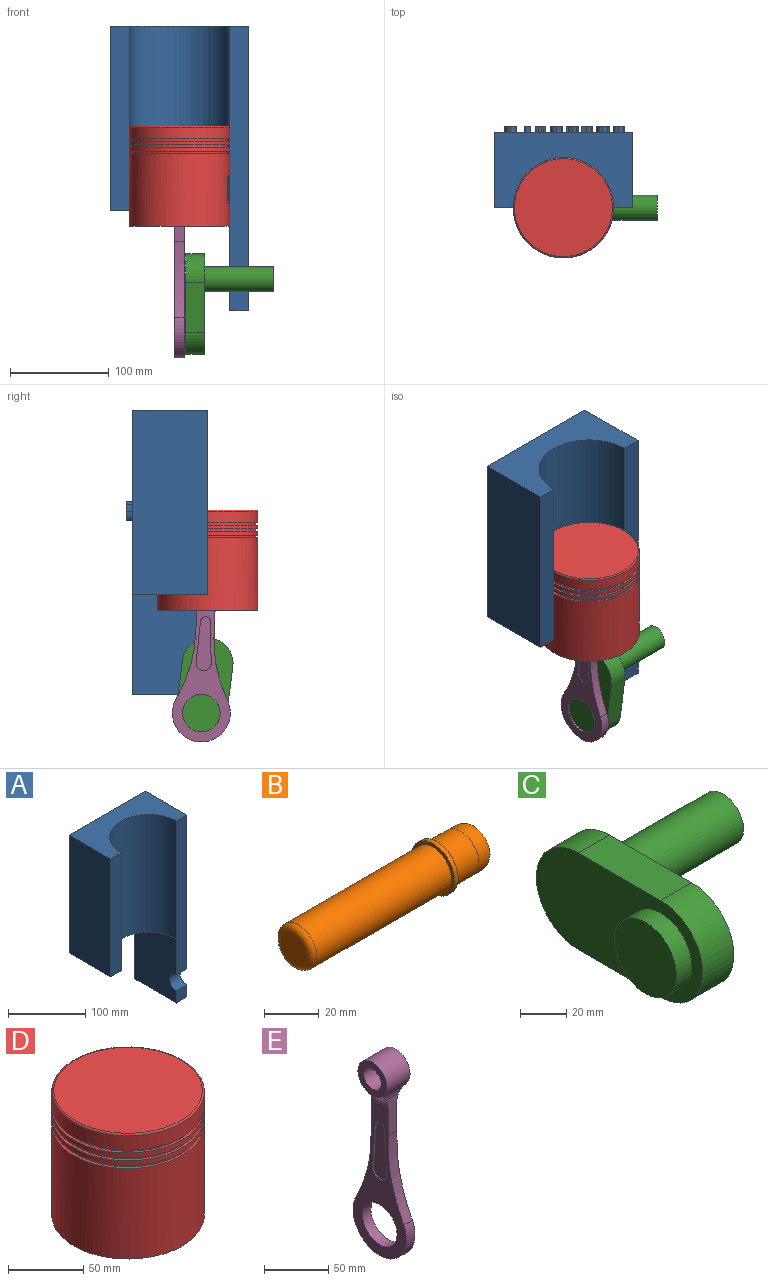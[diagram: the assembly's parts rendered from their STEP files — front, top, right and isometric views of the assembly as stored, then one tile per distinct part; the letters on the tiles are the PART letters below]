
ASSEMBLY  parts=5 mates=6
PART A: 146 faces, bbox 139.7x82.6x288.3 mm
  f0: plane 288.32x139.7mm, normal (0,1,0), area 27175.9mm2, adj f2,f3,f6,f8,f9,f10,f18,f19
  f1: plane 243.87x19.05mm, normal (0,-1,0), area 4645.6mm2, adj f2,f4,f8,f9,f11
  f2: plane 288.32x76.2mm, normal (1,0,0), area 21716.3mm2, adj f0,f1,f5,f8,f10,f11
  f3: plane 120.65x76.2mm, normal (0,0,-1), area 5139.9mm2, adj f0,f4,f6,f7,f9
  f4: cylinder r=50.8mm len=186.72mm, axis (0,0,-1), area 29798.5mm2, adj f1,f3,f7,f8
  f5: plane 19.05x19.05mm, normal (0,-1,0), area 362.9mm2, adj f2,f9,f10,f11
  f6: plane 186.72x76.2mm, normal (-1,0,0), area 14227.7mm2, adj f0,f3,f7,f8
  f7: plane 186.72x19.05mm, normal (0,-1,0), area 3556.9mm2, adj f3,f4,f6,f8
  f8: plane 139.7x76.2mm, normal (0,0,1), area 6591.5mm2, adj f0,f1,f2,f4,f6,f7
  f9: plane 101.6x76.2mm, normal (-1,0,0), area 7488.6mm2, adj f0,f1,f3,f5,f10,f11
  f10: plane 76.2x19.05mm, normal (0,0,-1), area 1451.6mm2, adj f0,f2,f5,f9
  f11: cylinder r=12.7mm len=25.4mm, axis (1,0,0), area 760.1mm2, adj f1,f2,f5,f9
  f12: plane 6.35x2.06mm, normal (-0.04,0,-1), area 13.1mm2, adj f13,f35,f36,f37
  f13: plane 6.35x1.26mm, normal (1,0,0), area 8mm2, adj f12,f14,f36,f37
  f14: extruded ~6.35x2.92mm, area 20.4mm2, adj f13,f15,f36,f37
  f15: extruded ~6.35x2.98mm, area 20.5mm2, adj f14,f16,f36,f37
  f16: extruded ~6.35x2.54mm, area 24.8mm2, adj f15,f17,f36,f37
  f17: extruded ~6.35x2.08mm, area 15.4mm2, adj f16,f35,f36,f37
  f18: plane 6.35x1.93mm, normal (0.97,0,-0.24), area 12.6mm2, adj f0,f19,f34,f36
  f19: plane 6.35x1.66mm, normal (0,0,-1), area 10.6mm2, adj f0,f18,f20,f36
  f20: plane 9.56x6.35mm, normal (-1,0,0), area 60.7mm2, adj f0,f19,f21,f36
  f21: extruded ~6.35x3.55mm, area 24.7mm2, adj f0,f20,f22,f36
  f22: extruded ~6.35x4.17mm, area 28mm2, adj f0,f21,f23,f36
  f23: extruded ~6.35x4.87mm, area 32.2mm2, adj f0,f22,f24,f36
  f24: plane 6.35x1.74mm, normal (0.91,0,-0.42), area 12.2mm2, adj f0,f23,f25,f36
  f25: extruded ~6.35x4.17mm, area 27.5mm2, adj f0,f24,f26,f36
  f26: extruded ~6.35x3.1mm, area 31.4mm2, adj f0,f25,f27,f36
  f27: plane 6.35x0.87mm, normal (1,0,0), area 5.6mm2, adj f0,f26,f28,f36
  f28: plane 6.35x2.58mm, normal (0.03,0,1), area 16.4mm2, adj f0,f27,f29,f36
  f29: extruded ~6.48x6.35mm, area 56.1mm2, adj f0,f28,f30,f36
  f30: extruded ~6.35x3.06mm, area 21.5mm2, adj f0,f29,f31,f36
  f31: extruded ~6.35x3.25mm, area 22.3mm2, adj f0,f30,f32,f36
  f32: extruded ~6.35x2.66mm, area 17.3mm2, adj f0,f31,f33,f36
  f33: extruded ~6.35x2.01mm, area 16.9mm2, adj f0,f32,f34,f36
  f34: plane 6.35x0.1mm, normal (0,0,-1), area 0.6mm2, adj f0,f18,f33,f36
  f35: extruded ~6.35x3.53mm, area 23.2mm2, adj f12,f17,f36,f37
  f36: plane 14.47x11.32mm, normal (0,1,0), area 83mm2, adj f12,f13,f14,f15,f16,f17,f18,f19
  f37: plane 6.63x5.21mm, normal (0,1,0), area 27.9mm2, adj f12,f13,f14,f15,f16,f17,f35
  f38: plane 7.28x6.35mm, normal (0,0,1), area 46.2mm2, adj f39,f52,f53,f54
  f39: extruded ~6.35x3.88mm, area 38.9mm2, adj f38,f52,f53,f54
  f40: plane 9.84x6.35mm, normal (0,0,-1), area 62.5mm2, adj f0,f41,f51,f53
  f41: plane 6.35x1.44mm, normal (-1,0,0), area 9.1mm2, adj f0,f40,f42,f53
  f42: extruded ~6.35x4.54mm, area 31.4mm2, adj f0,f41,f43,f53
  f43: extruded ~6.35x4.3mm, area 30.3mm2, adj f0,f42,f44,f53
  f44: extruded ~6.35x4.61mm, area 32.9mm2, adj f0,f43,f45,f53
  f45: extruded ~6.35x5.36mm, area 36.5mm2, adj f0,f44,f46,f53
  f46: extruded ~6.35x5.23mm, area 36.2mm2, adj f0,f45,f47,f53
  f47: extruded ~6.35x4.98mm, area 34.8mm2, adj f0,f46,f48,f53
  f48: extruded ~6.35x4.63mm, area 30.2mm2, adj f0,f47,f49,f53
  f49: plane 6.35x2.03mm, normal (-1,0,0), area 12.9mm2, adj f0,f48,f50,f53
  f50: extruded ~6.35x4.71mm, area 30.7mm2, adj f0,f49,f51,f53
  f51: extruded ~6.35x4.77mm, area 46.9mm2, adj f0,f40,f50,f53
  f52: extruded ~6.35x3.88mm, area 37.8mm2, adj f38,f39,f53,f54
  f53: plane 14.47x12.24mm, normal (0,1,0), area 84.4mm2, adj f38,f39,f40,f41,f42,f43,f44,f45
  f54: plane 7.28x3.88mm, normal (0,1,0), area 23.1mm2, adj f38,f39,f52
  f55: plane 6.35x3.41mm, normal (0.08,0,-1), area 21.7mm2, adj f0,f56,f64,f65
  f56: plane 16.14x6.35mm, normal (1,0,0), area 102.5mm2, adj f0,f55,f57,f65
  f57: plane 6.35x4.37mm, normal (0.06,0,1), area 27.8mm2, adj f0,f56,f58,f65
  f58: plane 6.35x1.56mm, normal (1,0,0), area 9.9mm2, adj f0,f57,f59,f65
  f59: plane 11.17x6.35mm, normal (0,0,-1), area 70.9mm2, adj f0,f58,f60,f65
  f60: plane 6.35x1.56mm, normal (-1,0,0), area 9.9mm2, adj f0,f59,f61,f65
  f61: plane 6.35x4.47mm, normal (-0.06,0,1), area 28.5mm2, adj f0,f60,f62,f65
  f62: plane 17.96x6.35mm, normal (-1,0,0), area 114.1mm2, adj f0,f61,f63,f65
  f63: plane 6.35x5.73mm, normal (0,0,1), area 36.4mm2, adj f0,f62,f64,f65
  f64: plane 6.35x1.55mm, normal (1,0,0), area 9.9mm2, adj f0,f55,f63,f65
  f65: plane 19.78x11.17mm, normal (0,1,0), area 66.6mm2, adj f55,f56,f57,f58,f59,f60,f61,f62
  f66: plane 6.35x0.52mm, normal (1,0,0), area 3.3mm2, adj f67,f86,f87,f88
  f67: extruded ~6.35x3.64mm, area 24.2mm2, adj f66,f68,f87,f88
  f68: extruded ~6.35x2.78mm, area 19.8mm2, adj f67,f69,f87,f88
  f69: extruded ~6.35x5.26mm, area 45.4mm2, adj f68,f70,f87,f88
  f70: extruded ~6.35x5.36mm, area 45.9mm2, adj f69,f71,f87,f88
  f71: extruded ~6.35x2.81mm, area 20.3mm2, adj f70,f86,f87,f88
  f72: plane 6.35x0.1mm, normal (0,0,-1), area 0.6mm2, adj f0,f73,f85,f87
  f73: plane 6.35x1.87mm, normal (0.98,0,-0.18), area 12.1mm2, adj f0,f72,f74,f87
  f74: plane 6.35x1.87mm, normal (0,0,-1), area 11.9mm2, adj f0,f73,f75,f87
  f75: plane 19.78x6.35mm, normal (-1,0,0), area 125.6mm2, adj f0,f74,f76,f87
  f76: plane 6.35x2.31mm, normal (0,0,1), area 14.7mm2, adj f0,f75,f77,f87
  f77: plane 6.35x5.54mm, normal (1,0,0), area 35.2mm2, adj f0,f76,f78,f87
  f78: extruded ~6.35x2.06mm, area 13.1mm2, adj f0,f77,f79,f87
  f79: plane 6.35x0.15mm, normal (0,0,1), area 1mm2, adj f0,f78,f80,f87
  f80: extruded ~6.35x4.09mm, area 30.2mm2, adj f0,f79,f81,f87
  f81: extruded ~6.35x4mm, area 29.3mm2, adj f0,f80,f82,f87
  f82: extruded ~6.35x5.35mm, area 35.8mm2, adj f0,f81,f83,f87
  f83: extruded ~6.35x5.31mm, area 35.6mm2, adj f0,f82,f84,f87
  f84: extruded ~6.35x4.01mm, area 29.3mm2, adj f0,f83,f85,f87
  f85: extruded ~6.35x4.09mm, area 30.6mm2, adj f0,f72,f84,f87
  f86: extruded ~6.35x4.11mm, area 27.1mm2, adj f66,f71,f87,f88
  f87: plane 20.04x11.87mm, normal (0,1,0), area 100mm2, adj f66,f67,f68,f69,f70,f71,f72,f73
  f88: plane 10.63x7.15mm, normal (0,1,0), area 64.1mm2, adj f66,f67,f68,f69,f70,f71,f86
  f89: plane 7.28x6.35mm, normal (0,0,1), area 46.2mm2, adj f90,f103,f104,f105
  f90: extruded ~6.35x3.88mm, area 38.9mm2, adj f89,f103,f104,f105
  f91: plane 9.84x6.35mm, normal (0,0,-1), area 62.5mm2, adj f0,f92,f102,f104
  f92: plane 6.35x1.44mm, normal (-1,0,0), area 9.1mm2, adj f0,f91,f93,f104
  f93: extruded ~6.35x4.54mm, area 31.4mm2, adj f0,f92,f94,f104
  f94: extruded ~6.35x4.3mm, area 30.3mm2, adj f0,f93,f95,f104
  f95: extruded ~6.35x4.61mm, area 32.9mm2, adj f0,f94,f96,f104
  f96: extruded ~6.35x5.36mm, area 36.5mm2, adj f0,f95,f97,f104
  f97: extruded ~6.35x5.23mm, area 36.2mm2, adj f0,f96,f98,f104
  f98: extruded ~6.35x4.98mm, area 34.8mm2, adj f0,f97,f99,f104
  f99: extruded ~6.35x4.63mm, area 30.2mm2, adj f0,f98,f100,f104
  f100: plane 6.35x2.03mm, normal (-1,0,0), area 12.9mm2, adj f0,f99,f101,f104
  f101: extruded ~6.35x4.71mm, area 30.7mm2, adj f0,f100,f102,f104
  f102: extruded ~6.35x4.77mm, area 46.9mm2, adj f0,f91,f101,f104
  f103: extruded ~6.35x3.88mm, area 37.8mm2, adj f89,f90,f104,f105
  f104: plane 14.47x12.24mm, normal (0,1,0), area 84.4mm2, adj f89,f90,f91,f92,f93,f94,f95,f96
  f105: plane 7.28x3.88mm, normal (0,1,0), area 23.1mm2, adj f89,f90,f103
  f106: plane 6.35x2.11mm, normal (-0.96,0,-0.28), area 14mm2, adj f0,f107,f118,f119
  f107: extruded ~6.35x3.05mm, area 19.8mm2, adj f0,f106,f108,f119
  f108: extruded ~6.35x2.72mm, area 17.9mm2, adj f0,f107,f109,f119
  f109: extruded ~6.35x2.16mm, area 19.2mm2, adj f0,f108,f110,f119
  f110: plane 6.35x0.1mm, normal (0,0,1), area 0.6mm2, adj f0,f109,f111,f119
  f111: plane 6.35x2.55mm, normal (-0.99,0,0.11), area 16.3mm2, adj f0,f110,f112,f119
  f112: plane 6.35x1.88mm, normal (0,0,1), area 12mm2, adj f0,f111,f113,f119
  f113: plane 13.95x6.35mm, normal (1,0,0), area 88.6mm2, adj f0,f112,f114,f119
  f114: plane 6.35x2.31mm, normal (0,0,-1), area 14.7mm2, adj f0,f113,f115,f119
  f115: plane 7.52x6.35mm, normal (-1,0,0), area 47.8mm2, adj f0,f114,f116,f119
  f116: extruded ~6.35x3.4mm, area 23.3mm2, adj f0,f115,f117,f119
  f117: extruded ~6.35x3.2mm, area 22.2mm2, adj f0,f116,f118,f119
  f118: extruded ~6.35x2.85mm, area 18.5mm2, adj f0,f106,f117,f119
  f119: plane 14.21x10.1mm, normal (0,1,0), area 47.5mm2, adj f106,f107,f108,f109,f110,f111,f112,f113
  f120: plane 6.35x2.24mm, normal (0,0,-1), area 14.2mm2, adj f0,f121,f128,f129
  f121: plane 18.58x6.35mm, normal (-1,0,0), area 118mm2, adj f0,f120,f122,f129
  f122: plane 6.35x1.91mm, normal (0,0,1), area 12.1mm2, adj f0,f121,f123,f129
  f123: plane 6.35x4.87mm, normal (0.62,0,0.79), area 39.2mm2, adj f0,f122,f124,f129
  f124: plane 6.35x1.56mm, normal (0.79,0,-0.62), area 12.6mm2, adj f0,f123,f125,f129
  f125: plane 6.35x1.87mm, normal (-0.63,0,-0.77), area 15.4mm2, adj f0,f124,f126,f129
  f126: extruded ~6.35x1.54mm, area 13.4mm2, adj f0,f125,f127,f129
  f127: extruded ~6.35x4.59mm, area 29.1mm2, adj f0,f126,f128,f129
  f128: plane 11.6x6.35mm, normal (1,0,0), area 73.7mm2, adj f0,f120,f127,f129
  f129: plane 18.58x6.78mm, normal (0,1,0), area 51mm2, adj f120,f121,f122,f123,f124,f125,f126,f127
  f130: extruded ~6.35x2.74mm, area 22.1mm2, adj f131,f143,f144,f145
  f131: extruded ~6.35x2.7mm, area 21.8mm2, adj f130,f132,f144,f145
  f132: extruded ~6.35x5.82mm, area 37.6mm2, adj f131,f133,f144,f145
  f133: extruded ~6.35x5.8mm, area 37.5mm2, adj f132,f134,f144,f145
  f134: extruded ~6.35x2.7mm, area 21.8mm2, adj f133,f135,f144,f145
  f135: extruded ~6.35x2.74mm, area 22.1mm2, adj f134,f136,f144,f145
  f136: extruded ~6.35x5.79mm, area 37.4mm2, adj f135,f143,f144,f145
  f137: extruded ~6.35x4.41mm, area 33.7mm2, adj f0,f138,f142,f144
  f138: extruded ~9.57x6.35mm, area 80.9mm2, adj f0,f137,f139,f144
  f139: extruded ~7.1x6.35mm, area 46.6mm2, adj f0,f138,f140,f144
  f140: extruded ~6.35x4.45mm, area 33.9mm2, adj f0,f139,f141,f144
  f141: extruded ~9.56x6.35mm, area 80.6mm2, adj f0,f140,f142,f144
  f142: extruded ~7.11x6.35mm, area 46.7mm2, adj f0,f137,f141,f144
  f143: extruded ~6.35x5.82mm, area 37.6mm2, adj f130,f136,f144,f145
  f144: plane 19.13x11.87mm, normal (0,1,0), area 96.6mm2, adj f130,f131,f132,f133,f134,f135,f136,f137
  f145: plane 15.18x7.18mm, normal (0,1,0), area 92.1mm2, adj f130,f131,f132,f133,f134,f135,f136,f143
PART B: 9 faces, bbox 94x22.2x22.2 mm
  f0: cylinder r=9.53mm len=19.05mm, axis (-1,0,0), area 737.3mm2, adj f3,f8
  f1: plane 3.81x3.81mm, normal (1,0,0), area 11.4mm2, adj f8
  f2: cylinder r=11.11mm len=22.23mm, axis (-1,0,0), area 133mm2, adj f3,f4
  f3: plane 22.23x22.23mm, normal (1,0,0), area 102.9mm2, adj f0,f2
  f4: plane 22.23x22.23mm, normal (-1,0,0), area 102.9mm2, adj f2,f6
  f5: plane 13.97x13.97mm, normal (-1,0,0), area 153.3mm2, adj f7
  f6: cylinder r=9.53mm len=69.6mm, axis (-1,0,0), area 4165.1mm2, adj f4,f7
  f7: torus R=6.99mm, axis (1,0,0), area 215.6mm2, adj f5,f6
  f8: bspline ~19.05x19.05mm, area 631.1mm2, adj f0,f1
PART C: 10 faces, bbox 98.3x102.2x51.4 mm
  f0: cylinder r=19.05mm len=38.1mm, axis (1,0,0), area 1131mm2, adj f1,f7
  f1: plane 38.1x38.1mm, normal (-1,0,0), area 1140.1mm2, adj f0
  f2: cylinder r=25.72mm len=51.44mm, axis (-1,0,0), area 1539.1mm2, adj f3,f5,f6,f7
  f3: plane 50.8x19.05mm, normal (0,0,-1), area 967.7mm2, adj f2,f4,f6,f7
  f4: cylinder r=25.72mm len=51.44mm, axis (-1,0,0), area 1539.1mm2, adj f3,f5,f6,f7
  f5: plane 50.8x19.05mm, normal (0,0,1), area 967.7mm2, adj f2,f4,f6,f7
  f6: plane 102.24x51.44mm, normal (1,0,0), area 4184.1mm2, adj f2,f3,f4,f5,f8
  f7: plane 102.24x51.44mm, normal (-1,0,0), area 3550.7mm2, adj f0,f2,f3,f4,f5
  f8: cylinder r=12.7mm len=69.85mm, axis (-1,0,0), area 5573.8mm2, adj f6,f9
  f9: plane 25.4x25.4mm, normal (1,0,0), area 506.7mm2, adj f8
PART D: 39 faces, bbox 110.4x110.4x102.1 mm
  f0: cylinder r=9.53mm len=19.05mm, axis (1,0,0), area 1003.3mm2, adj f25,f32
  f1: cylinder r=50.8mm len=101.6mm, axis (0,0,1), area 22639.7mm2, adj f14,f24,f33,f34,f36,f37
  f2: cylinder r=9.53mm len=19.05mm, axis (1,0,0), area 896.9mm2, adj f23,f26
  f3: cylinder r=50.8mm len=101.6mm, axis (0,0,1), area 1216.1mm2, adj f5,f13
  f4: plane 101.6x101.6mm, normal (0,0,-1), area 660mm2, adj f6,f12
  f5: plane 101.6x101.6mm, normal (0,0,1), area 660.2mm2, adj f3,f6
  f6: cylinder r=48.68mm len=97.36mm, axis (0,0,-1), area 776.9mm2, adj f4,f5
  f7: plane 99.06x99.06mm, normal (0,0,1), area 7707mm2, adj f38
  f8: cylinder r=50.8mm len=101.6mm, axis (0,0,1), area 3648.3mm2, adj f9,f38
  f9: plane 101.6x101.6mm, normal (0,0,-1), area 659.2mm2, adj f8,f10
  f10: cylinder r=48.68mm len=97.36mm, axis (0,0,-1), area 776.9mm2, adj f9,f11
  f11: plane 101.6x101.6mm, normal (0,0,1), area 660.2mm2, adj f10,f12
  f12: cylinder r=50.8mm len=101.6mm, axis (0,0,1), area 1216.1mm2, adj f4,f11
  f13: plane 101.6x101.6mm, normal (0,0,-1), area 660mm2, adj f3,f15
  f14: plane 101.6x101.6mm, normal (0,0,1), area 659.2mm2, adj f1,f15
  f15: cylinder r=48.68mm len=97.36mm, axis (0,0,-1), area 776.9mm2, adj f13,f14
  f16: plane 19.05x19.05mm, normal (1,0,0), area 285mm2, adj f17
  f17: cylinder r=9.53mm len=31.75mm, axis (1,0,0), area 1900.2mm2, adj f16,f18
  f18: plane 25.4x25.4mm, normal (1,0,0), area 221.7mm2, adj f17,f20
  f19: plane 88.9x88.9mm, normal (0,0,-1), area 6207.2mm2, adj f22
  f20: cylinder r=12.7mm len=26.67mm, axis (-1,0,0), area 1535mm2, adj f18,f31
  f21: cylinder r=12.7mm len=26.67mm, axis (1,0,0), area 1535mm2, adj f23,f30
  f22: cylinder r=44.45mm len=91.44mm, axis (0,0,1), area 17592.5mm2, adj f19,f24,f30,f31
  f23: plane 25.4x25.4mm, normal (-1,0,0), area 221.7mm2, adj f2,f21
  f24: plane 101.6x101.6mm, normal (0,0,-1), area 1900.2mm2, adj f1,f22
  f25: plane 22.23x22.23mm, normal (-1,0,0), area 102.9mm2, adj f0,f27
  f26: plane 22.23x22.23mm, normal (1,0,0), area 102.9mm2, adj f2,f27
  f27: cylinder r=11.11mm len=22.23mm, axis (-1,0,0), area 177.3mm2, adj f25,f26
  f28: plane 31.79x25.48mm, normal (1,0,0), area 391.5mm2, adj f29,f32,f33,f34,f35,f36
  f29: plane 22.29x1.27mm, normal (0,0,1), area 18.9mm2, adj f28,f33
  f30: bspline ~71.45x63.25mm, area 3529.9mm2, adj f21,f22
  f31: bspline ~71.49x63.32mm, area 3529.4mm2, adj f20,f22
  f32: torus R=10.79mm, axis (1,0,0), area 125.2mm2, adj f0,f28
  f33: torus R=49.53mm, axis (0,0,1), area 56.3mm2, adj f1,f28,f29,f34,f36
  f34: cylinder r=1.27mm len=25.4mm, axis (0,0,1), area 10.3mm2, adj f1,f28,f33,f37
  f35: cylinder r=1.27mm len=31.32mm, axis (0,-1,0), area 31.2mm2, adj f28,f37
  f36: cylinder r=1.27mm len=25.4mm, axis (0,0,1), area 10.3mm2, adj f1,f28,f33,f37
  f37: bspline ~32.12x2.69mm, area 50.1mm2, adj f1,f34,f35,f36
  f38: torus R=49.53mm, axis (0,0,1), area 631mm2, adj f7,f8
PART E: 26 faces, bbox 35.2x61.2x187.8 mm
  f0: cylinder r=9.53mm len=25.4mm, axis (-1,0,0), area 1520.1mm2, adj f2,f3
  f1: cylinder r=15.88mm len=31.75mm, axis (-1,0,0), area 1829.5mm2, adj f2,f3,f8,f11
  f2: plane 31.75x31.75mm, normal (1,0,0), area 506.7mm2, adj f0,f1,f10
  f3: plane 31.75x31.75mm, normal (-1,0,0), area 506.7mm2, adj f0,f1,f9
  f4: plane 35.2x14.16mm, normal (0,-1,0), area 340mm2, adj f6,f7,f8,f9,f10,f14
  f5: plane 35.2x14.16mm, normal (0,1,0), area 340mm2, adj f6,f7,f9,f10,f11,f15
  f6: plane 145.49x58.64mm, normal (1,0,0), area 2910.8mm2, adj f4,f5,f10,f12,f13,f14,f15,f21
  f7: plane 145.49x58.64mm, normal (-1,0,0), area 2910.8mm2, adj f4,f5,f9,f12,f13,f14,f15,f16
  f8: cylinder r=12.7mm len=25.4mm, axis (-1,0,0), area 173.8mm2, adj f1,f4,f9,f10
  f9: torus R=27.67mm, axis (-1,0,0), area 323.1mm2, adj f3,f4,f5,f7,f8,f11
  f10: torus R=27.67mm, axis (-1,0,0), area 323.1mm2, adj f2,f4,f5,f6,f8,f11
  f11: cylinder r=12.7mm len=25.4mm, axis (-1,0,0), area 173.8mm2, adj f1,f5,f9,f10
  f12: cylinder r=29.31mm len=58.63mm, axis (-1,0,0), area 1115mm2, adj f6,f7,f14,f15
  f13: cylinder r=19.05mm len=38.1mm, axis (-1,0,0), area 1129.5mm2, adj f6,f7
  f14: bspline ~76.44x17.27mm, area 748.3mm2, adj f4,f6,f7,f12
  f15: bspline ~76.44x17.27mm, area 748.3mm2, adj f5,f6,f7,f12
  f16: plane 41.88x2.53mm, normal (0,1,-0.06), area 53.3mm2, adj f7,f17,f19,f20
  f17: cylinder r=5.09mm len=10.16mm, axis (-1,0,0), area 19.5mm2, adj f7,f16,f18,f20
  f18: plane 41.88x2.53mm, normal (0,-1,-0.06), area 53.3mm2, adj f7,f17,f19,f20
  f19: cylinder r=7.62mm len=15.25mm, axis (-1,0,0), area 31.6mm2, adj f7,f16,f18,f20
  f20: plane 54.75x15.25mm, normal (-1,0,0), area 667.4mm2, adj f16,f17,f18,f19
  f21: plane 41.88x2.53mm, normal (0,1,-0.06), area 53.3mm2, adj f6,f22,f24,f25
  f22: cylinder r=7.62mm len=15.25mm, axis (1,0,0), area 31.6mm2, adj f6,f21,f23,f25
  f23: plane 41.88x2.53mm, normal (0,-1,-0.06), area 53.3mm2, adj f6,f22,f24,f25
  f24: cylinder r=5.09mm len=10.16mm, axis (1,0,0), area 19.5mm2, adj f6,f21,f23,f25
  f25: plane 54.75x15.25mm, normal (1,0,0), area 667.4mm2, adj f21,f22,f23,f24
PLACE A rot(axis=(0,0,-1),0deg) t=(-24.12,-150.17,-272.8)mm fixed
PLACE B t=(45.73,-150.17,-187.42)mm
PLACE C rot(axis=(1,0,0),97.2deg) t=(47.36,-347.89,-418.96)mm
PLACE D rot(axis=(0,0,-1),0deg) t=(45.73,-150.17,-187.42)mm
PLACE E rot(axis=(1,0,0),2.6deg) t=(45.73,-153.02,-187.49)mm
MATE slider D.f1 <-> A.f4  axis (0,0,1) through (45.73,-150.17,-188.69)mm
MATE fastened B.f0 <-> D.f0  axis (-1,0,0) through (1.28,-150.17,-250.92)mm
MATE cylindrical C.f0 <-> E.f12  axis (-1,0,0) through (42.63,-143.77,-393.04)mm
MATE revolute E.f0 <-> B.f0  axis (-1,0,0) through (45.73,-150.17,-250.92)mm
MATE revolute C.f4 <-> A.f11  axis (-1,0,0) through (106.05,-150.17,-342.65)mm
MATE cylindrical A.f4 <-> D.f1  axis (0,0,-1) through (45.73,-150.17,-179.44)mm
